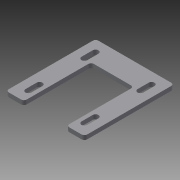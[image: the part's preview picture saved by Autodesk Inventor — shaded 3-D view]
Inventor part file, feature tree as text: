
AUTODESK INVENTOR PART (.ipt)
format: ipt  version: 2013 (Build 170138000, 138)  size: 117,248 bytes
history: native  units: in
note: dims shown in document units (in); Inventor stores cm internally (conversion verified against a paired STEP export)
features: extrude x1, fillet x1, mirror x1, sketch x1
ambient origin geometry x8: Origin, YZ Plane, XZ Plane, XY Plane, X Axis, Y Axis, Z Axis, Center Point
bodies: Solid1 (feature_tree)
feature tree (4):
  extrude  "Extrusion1"  Depth=0.1875in TaperAngle=0.0deg
  fillet  "Fillet1"  Radius=1.75in
  mirror  "Mirror2"
  sketch  "Sketch1"  dims[d1=4.0in d6=0.1875in d7=0.0in d8=1.75in d9=1.0in d11=0.26in d14=0.5in d15=0.5in d16=0.26in d17=0.5in d18=0.5in d19=0.8in d20=0.125in d21=1.25in]
